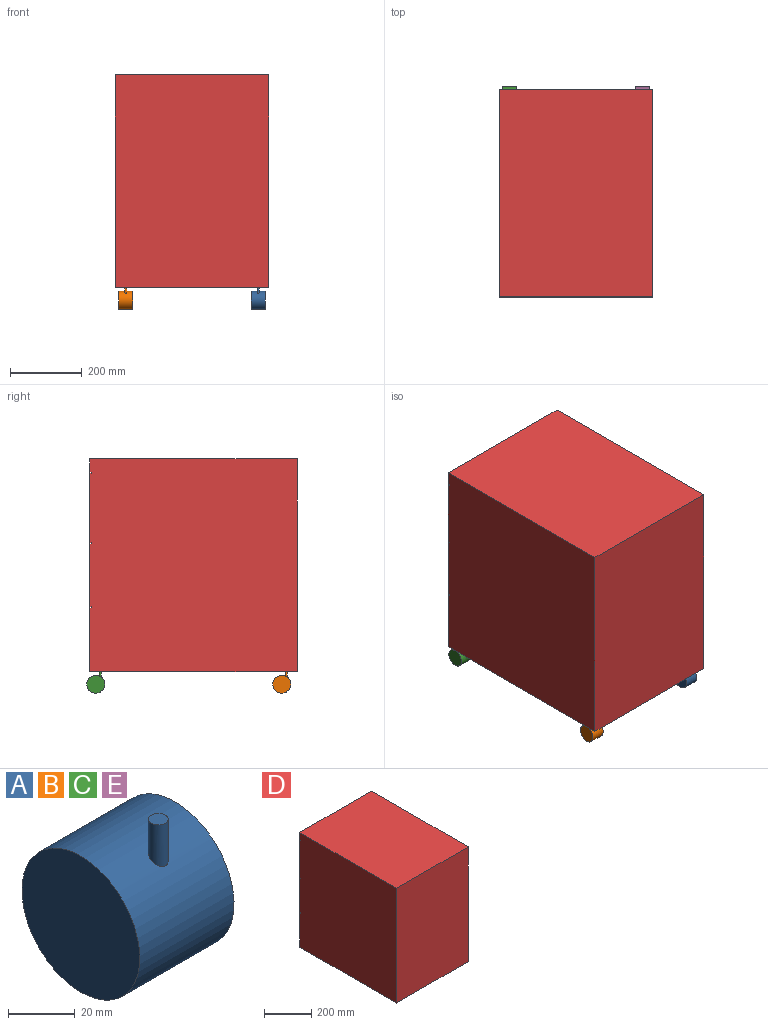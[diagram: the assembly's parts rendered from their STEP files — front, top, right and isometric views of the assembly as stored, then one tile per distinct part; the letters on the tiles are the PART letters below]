
ASSEMBLY  parts=5 mates=4
PART A: 5 faces, bbox 40x50x60 mm
  f0: cylinder r=25mm len=50mm, axis (-1,0,0), area 6250.3mm2, adj f1,f2,f3
  f1: plane 50x50mm, normal (1,0,0), area 1963.5mm2, adj f0
  f2: plane 50x50mm, normal (-1,0,0), area 1963.5mm2, adj f0
  f3: cylinder r=3mm len=15.65mm, axis (0,0,-1), area 257.9mm2, adj f0,f4
  f4: plane 6x6mm, normal (0,0,1), area 28.3mm2, adj f3
PART B: same geometry as A
PART C: same geometry as A
PART D: 18 faces, bbox 430x580x595 mm
  f0: plane 595x580mm, normal (-1,0,0), area 345070mm2, adj f1,f2,f4,f5,f6,f7,f8,f9
  f1: plane 580x430mm, normal (0,0,1), area 249400mm2, adj f0,f3,f7,f17
  f2: plane 580x430mm, normal (0,0,-1), area 249400mm2, adj f0,f3,f4,f17
  f3: plane 595x580mm, normal (1,0,0), area 345070mm2, adj f1,f2,f4,f5,f6,f7,f8,f9
  f4: plane 430x179mm, normal (0,1,0), area 76970mm2, adj f0,f2,f3,f14
  f5: plane 430x177mm, normal (0,1,0), area 76110mm2, adj f0,f3,f11,f15
  f6: plane 430x195mm, normal (0,1,0), area 83850mm2, adj f0,f3,f8,f12
  f7: plane 430x38mm, normal (0,1,0), area 16340mm2, adj f0,f1,f3,f9
  f8: plane 430x5mm, normal (0,0,1), area 2150mm2, adj f0,f3,f6,f10
  f9: plane 430x5mm, normal (0,0,-1), area 2150mm2, adj f0,f3,f7,f10
  f10: plane 430x2mm, normal (0,1,0), area 860mm2, adj f0,f3,f8,f9
  f11: plane 430x5mm, normal (0,0,1), area 2150mm2, adj f0,f3,f5,f13
  f12: plane 430x5mm, normal (0,0,-1), area 2150mm2, adj f0,f3,f6,f13
  f13: plane 430x2mm, normal (0,1,0), area 860mm2, adj f0,f3,f11,f12
  f14: plane 430x5mm, normal (0,0,1), area 2150mm2, adj f0,f3,f4,f16
  f15: plane 430x5mm, normal (0,0,-1), area 2150mm2, adj f0,f3,f5,f16
  f16: plane 430x2mm, normal (0,1,0), area 860mm2, adj f0,f3,f14,f15
  f17: plane 595x430mm, normal (0,-1,0), area 255850mm2, adj f0,f1,f2,f3
PART E: same geometry as A
PLACE A t=(489.63,-511.85,115.47)mm
PLACE B t=(119.63,-511.85,115.47)mm
PLACE C t=(119.63,8.15,115.47)mm
PLACE D t=(109.63,-1134.68,150.47)mm
PLACE E t=(489.63,8.15,115.47)mm
MATE fastened B.f3 <-> D.f2  axis (0,0,1) through (139.63,-524.68,150.47)mm
MATE fastened D.f2 <-> C.f3  axis (0,0,1) through (139.63,-4.68,150.47)mm
MATE fastened D.f2 <-> A.f3  axis (0,0,1) through (509.63,-524.68,150.47)mm
MATE fastened D.f2 <-> E.f3  axis (0,0,1) through (509.63,-4.68,150.47)mm
